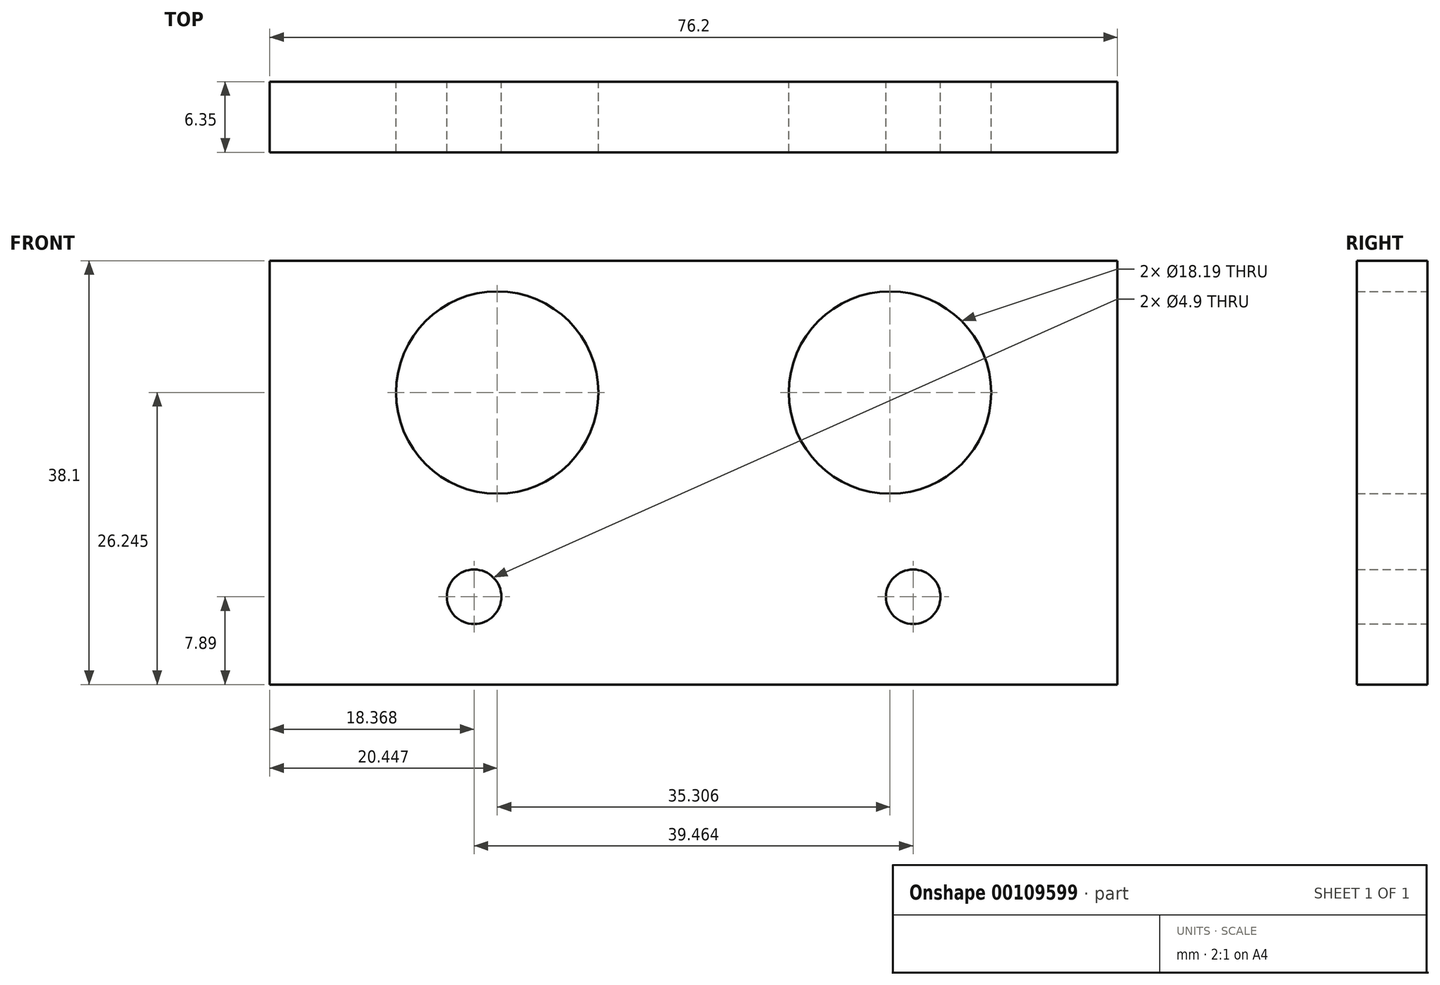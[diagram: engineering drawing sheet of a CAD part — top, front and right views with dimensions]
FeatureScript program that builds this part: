
annotation { "Feature Type Name" : "Feature", "Feature Type Description" : "" }
export const myFeature = defineFeature(function(context is Context, id is Id, definition is map)
    precondition{}
    {
        {
            var Q0;
            Q0=qCreatedBy(makeId("Front.planeOp"),FACE);
            var sketch = newSketch(context, id + "F0", { "sketchPlane" : qUnion([Q0])});
            skLineSegment(sketch, "E0.bottom", {"start": v(38.1, -19.05) * mm, "end": v(-38.1, -19.05) * mm});
            skLineSegment(sketch, "E0.top", {"start": v(38.1, 19.05) * mm, "end": v(-38.1, 19.05) * mm});
            skLineSegment(sketch, "E0.left", {"start": v(38.1, -19.05) * mm, "end": v(38.1, 19.05) * mm});
            skLineSegment(sketch, "E0.right", {"start": v(-38.1, -19.05) * mm, "end": v(-38.1, 19.05) * mm});
            skPoint(sketch, "E0.middle", {"position": v(0, 0) * mm});
            skCircle(sketch, "E1", {"center": v(-17.65, 7.2) * mm, "radius": 9.1 * mm});
            skLineSegment(sketch, "E2.bottom", {"start": v(2.17, 19.05) * mm, "end": v(-2.17, 19.05) * mm});
            skLineSegment(sketch, "E2.top", {"start": v(2.17, 82.55) * mm, "end": v(-2.17, 82.55) * mm});
            skLineSegment(sketch, "E2.left", {"start": v(2.17, 19.05) * mm, "end": v(2.17, 82.55) * mm});
            skLineSegment(sketch, "E2.right", {"start": v(-2.17, 19.05) * mm, "end": v(-2.17, 82.55) * mm});
            skPoint(sketch, "E2.middle", {"position": v(0, 50.8) * mm});
            skCircle(sketch, "E3", {"center": v(-19.73, -11.16) * mm, "radius": 2.45 * mm});
            skCircle(sketch, "E4.MirrorC", {"center": v(19.73, -11.16) * mm, "radius": 2.45 * mm});
            skCircle(sketch, "E5.MirrorC", {"center": v(17.65, 7.2) * mm, "radius": 9.1 * mm});
            skSolve(sketch);
        }
        {
            var Q0;
            Q0=makeQuery(id+"F0.imprint","IMPRINT",FACE,{"disambiguationData":[TD([[makeQuery(id+"F0.imprint","IMPRINT",EDGE,{"derivedFrom":sQuery(id+"F0.wireOp",EDGE,"E2.bottom")}),-1.0]])]});
            var Q1;
            Q1=makeQuery(id+"F0.imprint","IMPRINT",FACE,{"disambiguationData":[TD([[makeQuery(id+"F0.imprint","IMPRINT",EDGE,{"derivedFrom":sQuery(id+"F0.wireOp",EDGE,"E0.bottom")}),-1.0]])]});
            extrude(context, id + "F1", {"entities" : qUnion([Q0, Q1]), "depth" : 6.35 * mm});
        }
    });
